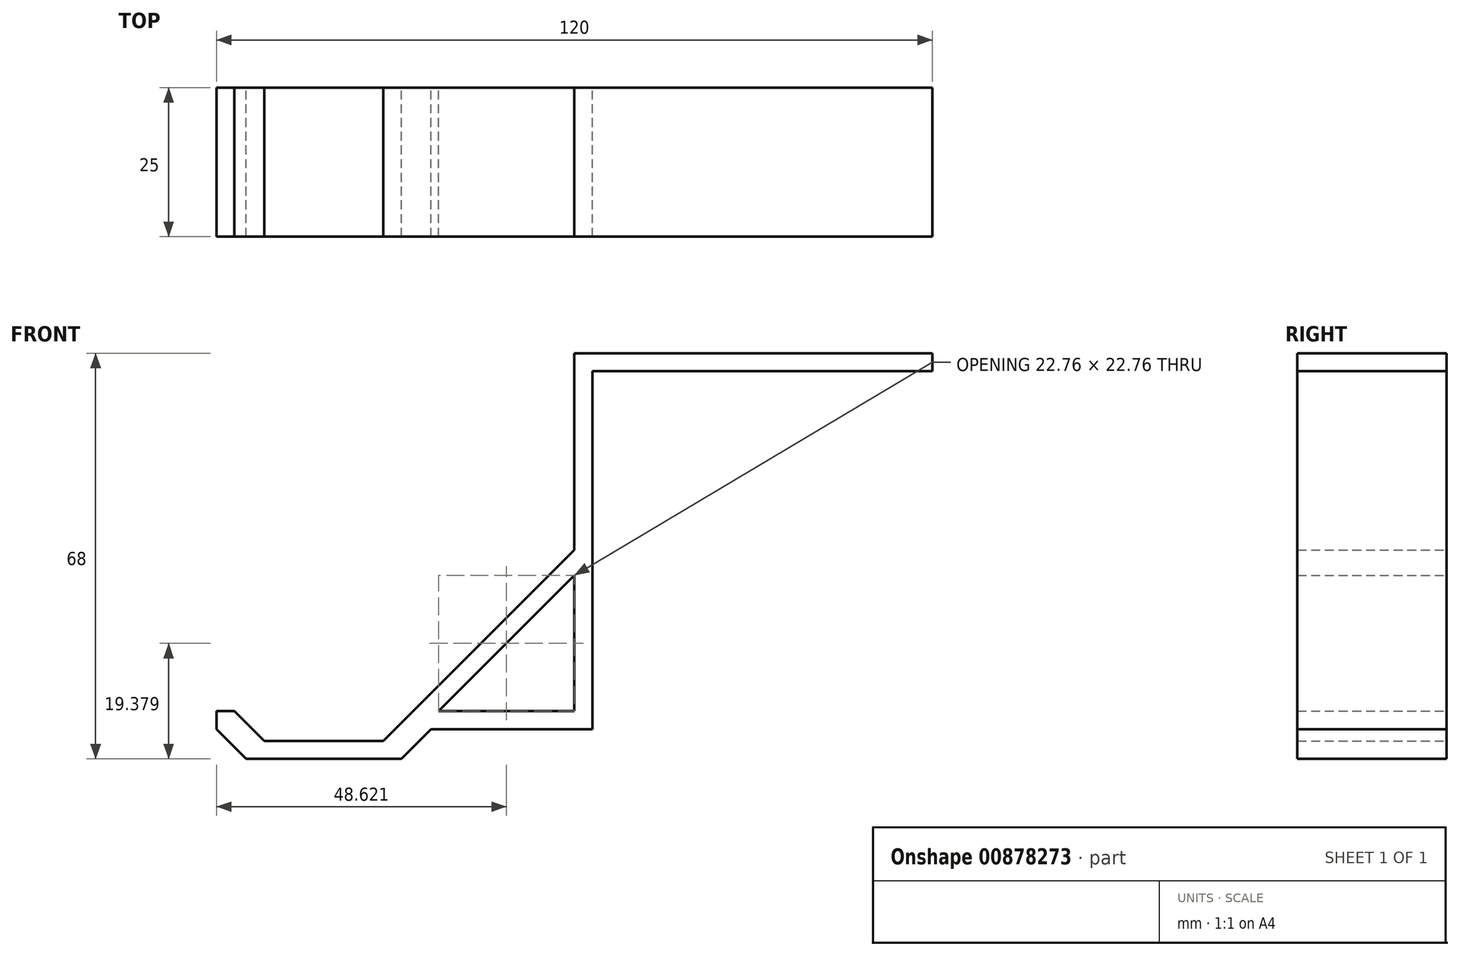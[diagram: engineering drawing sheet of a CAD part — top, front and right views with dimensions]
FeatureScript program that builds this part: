
annotation { "Feature Type Name" : "Feature", "Feature Type Description" : "" }
export const myFeature = defineFeature(function(context is Context, id is Id, definition is map)
    precondition{}
    {
        {
            var Q0;
            Q0=qCreatedBy(makeId("Front.planeOp"),FACE);
            var sketch = newSketch(context, id + "F0", { "sketchPlane" : qUnion([Q0])});
            skLineSegment(sketch, "E0", {"start": v(0, 0) * mm, "end": v(0, 60) * mm});
            skLineSegment(sketch, "E1", {"start": v(0, 60) * mm, "end": v(60, 60) * mm});
            skLineSegment(sketch, "E2", {"start": v(0, 0) * mm, "end": v(-32, 0) * mm});
            skLineSegment(sketch, "E3", {"start": v(-32, 0) * mm, "end": v(-32, -5) * mm});
            skLineSegment(sketch, "E4", {"start": v(-32, -5) * mm, "end": v(-57, -5) * mm});
            skLineSegment(sketch, "E5", {"start": v(-57, -5) * mm, "end": v(-57, 0) * mm});
            skLineSegment(sketch, "E6", {"start": v(-57, 0) * mm, "end": v(-60, 0) * mm});
            skLineSegment(sketch, "E7", {"start": v(-60, 0) * mm, "end": v(-60, -8) * mm});
            skLineSegment(sketch, "E8", {"start": v(-60, -8) * mm, "end": v(0, -8) * mm, "construction": true});
            skLineSegment(sketch, "E9", {"start": v(0, 0) * mm, "end": v(0, -8) * mm, "construction": true});
            skLineSegment(sketch, "E10", {"start": v(-29, -8) * mm, "end": v(-29, -3) * mm});
            skLineSegment(sketch, "E11", {"start": v(-29, -3) * mm, "end": v(0, -3) * mm});
            skLineSegment(sketch, "E12", {"start": v(60, 60) * mm, "end": v(60, 57) * mm});
            skLineSegment(sketch, "E13", {"start": v(60, 57) * mm, "end": v(3, 57) * mm});
            skLineSegment(sketch, "E14", {"start": v(3, 57) * mm, "end": v(3, -3) * mm});
            skLineSegment(sketch, "E15", {"start": v(3, -3) * mm, "end": v(0, -3) * mm});
            skLineSegment(sketch, "E16", {"start": v(-60, -8) * mm, "end": v(-29, -8) * mm});
            skLineSegment(sketch, "E17", {"start": v(-27, 0) * mm, "end": v(0, 27) * mm});
            skLineSegment(sketch, "E18", {"start": v(-22.76, 0) * mm, "end": v(0, 22.76) * mm});
            skSolve(sketch);
        }
        {
            var Q0;
            Q0 = qSketchRegion(id + "F0", true);
            extrude(context, id + "F1", {"entities" : qUnion([Q0]), "depth" : 25 * mm, "offsetDistance" : 25 * mm});
        }
        {
            var Q0;
            Q0=makeQuery(id+"F1.opExtrude","SWEPT_EDGE",EDGE,{"disambiguationData":[OSD([sQuery(id+"F0.wireOp",EDGE,"E4"),sQuery(id+"F0.wireOp",EDGE,"E5")])]});
            var Q1;
            Q1=makeQuery(id+"F1.opExtrude","SWEPT_EDGE",EDGE,{"disambiguationData":[OSD([sQuery(id+"F0.wireOp",EDGE,"E7"),sQuery(id+"F0.wireOp",EDGE,"E16")])]});
            var Q2;
            Q2=makeQuery(id+"F1.opExtrude","SWEPT_EDGE",EDGE,{"disambiguationData":[OSD([sQuery(id+"F0.wireOp",EDGE,"E10"),sQuery(id+"F0.wireOp",EDGE,"E11")])]});
            var Q3;
            Q3=makeQuery(id+"F1.opExtrude","SWEPT_EDGE",EDGE,{"disambiguationData":[OSD([sQuery(id+"F0.wireOp",EDGE,"E2"),sQuery(id+"F0.wireOp",EDGE,"E3")])]});
            chamfer(context, id + "F2", {"entities" : qUnion([Q0, Q1, Q2, Q3]), "width" : 5 * mm, "tangentPropagation" : true});
        }
    });
